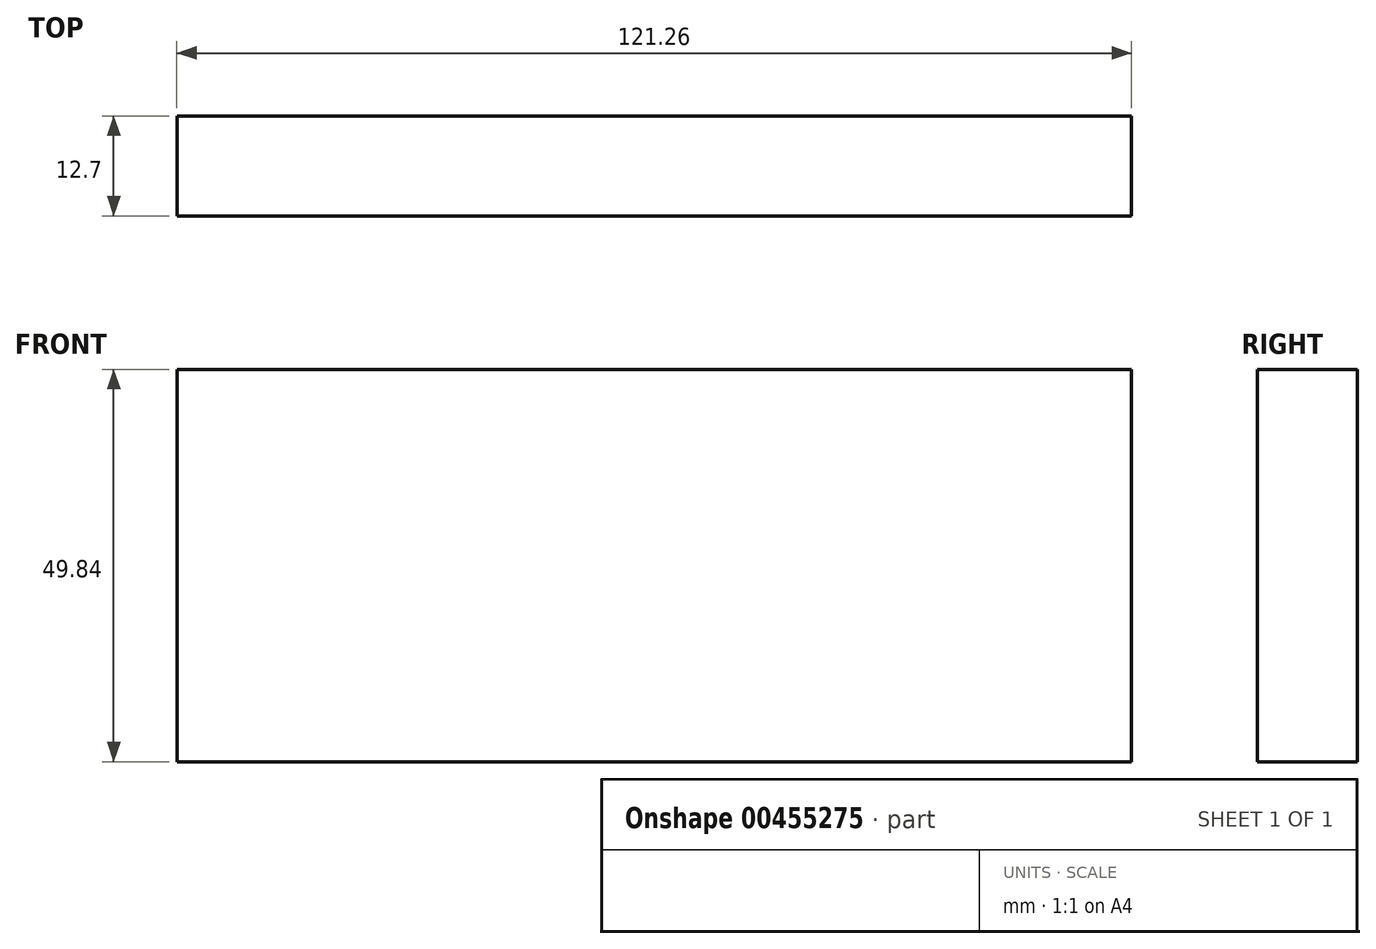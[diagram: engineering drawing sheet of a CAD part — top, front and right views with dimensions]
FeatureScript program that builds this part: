
annotation { "Feature Type Name" : "Feature", "Feature Type Description" : "" }
export const myFeature = defineFeature(function(context is Context, id is Id, definition is map)
    precondition{}
    {
        {
            var Q0;
            Q0=qCreatedBy(makeId("Front.planeOp"),FACE);
            var sketch = newSketch(context, id + "F0", { "sketchPlane" : qUnion([Q0])});
            skLineSegment(sketch, "E0.bottom", {"start": v(-60.63, 24.92) * mm, "end": v(60.63, 24.92) * mm});
            skLineSegment(sketch, "E0.top", {"start": v(-60.63, -24.92) * mm, "end": v(60.63, -24.92) * mm});
            skLineSegment(sketch, "E0.left", {"start": v(-60.63, 24.92) * mm, "end": v(-60.63, -24.92) * mm});
            skLineSegment(sketch, "E0.right", {"start": v(60.63, 24.92) * mm, "end": v(60.63, -24.92) * mm});
            skPoint(sketch, "E0.middle", {"position": v(0, 0) * mm});
            skSolve(sketch);
        }
        {
            var Q0;
            Q0 = qSketchRegion(id + "F0", true);
            extrude(context, id + "F1", {"entities" : qUnion([Q0]), "endBound" : BoundingType.SYMMETRIC, "depth" : 12.7 * mm});
        }
    });
